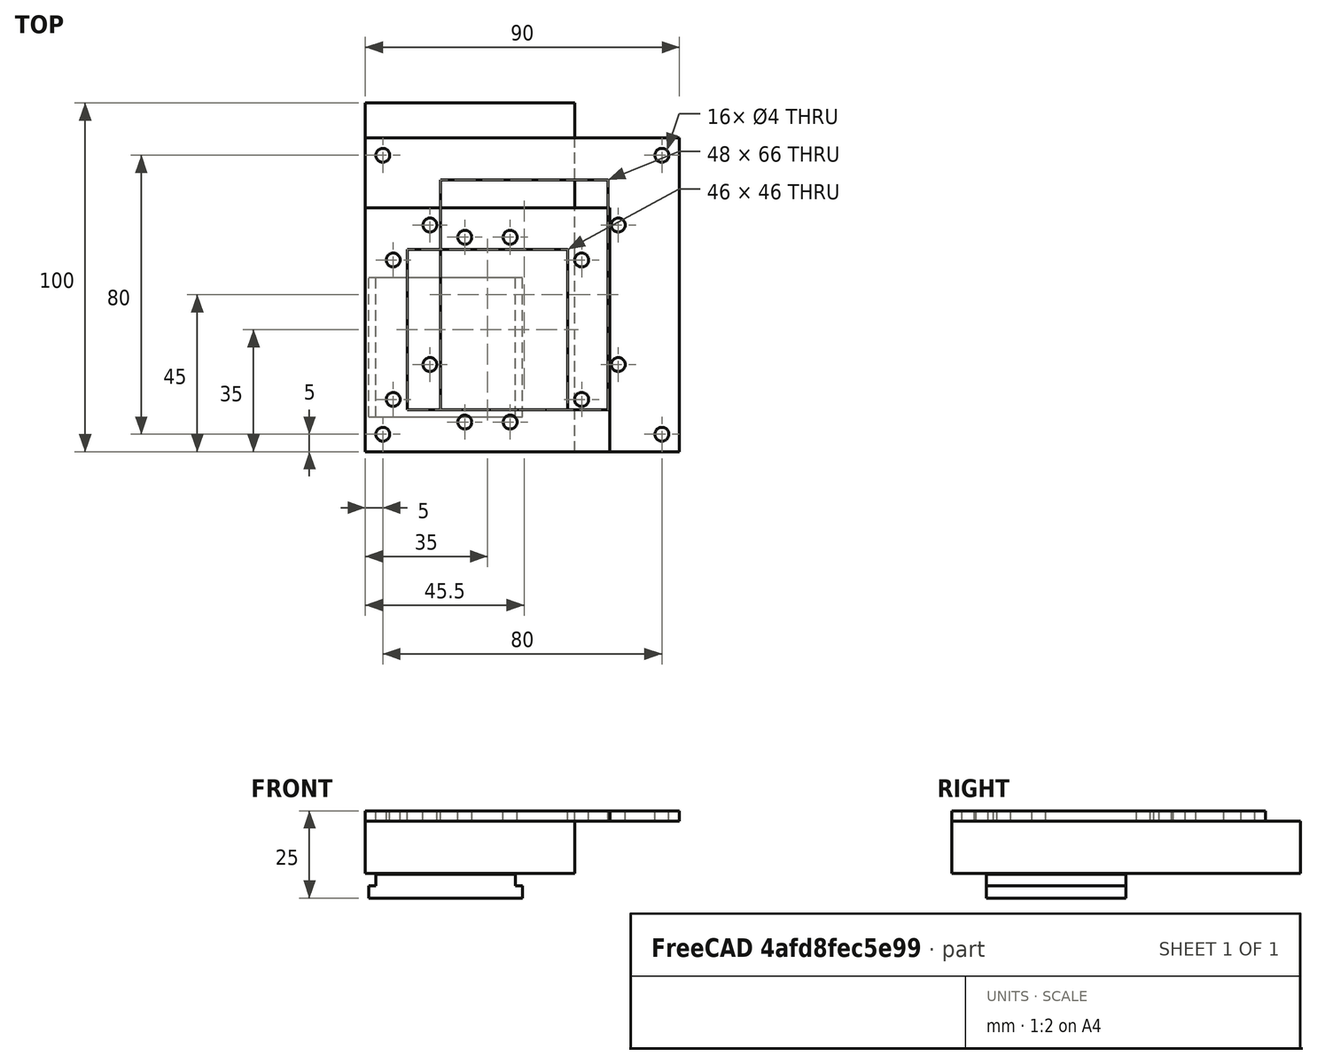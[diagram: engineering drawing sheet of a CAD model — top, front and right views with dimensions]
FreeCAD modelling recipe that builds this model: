
FCSTD DOCUMENT  (FreeCAD 0.18.4R)
Label: box_with_cone_less_holes
License: All rights reserved
LicenseURL: http://en.wikipedia.org/wiki/All_rights_reserved
objects: Part::FeaturePython×9, Part::Box×8, Path::FeaturePython×7, Part::Cylinder×6, Part::Cut×6, Part::MultiFuse×4, App::Part×4, Part::Cone×2, Part::Fuse×1, App::FeaturePython×1, App::DocumentObjectGroup×1, Path::FeatureCompoundPython×1
note: 39 computed .brp shape members not serialized (recipe doc carries the construction recipe); baked Part::Feature solids carry a one-line shape summary decoded from their .brp

FEATURE [Part::Box] Box  label="Cube"
  AttacherType = Attacher::AttachEngine3D
  Height = 15
  Length = 46
  Placement = pos=(0,0,-15) rot=(0,0,1;0rad)
  Width = 60
FEATURE [Part::Cone] Cone  label="top cone"
  Angle = 360
  AttacherType = Attacher::AttachEngine3D
  Height = 7
  Placement = pos=(0,0,-7) rot=(0,0,1;0rad)
  Radius1 = 2.8
  Radius2 = 3
FEATURE [Part::Cone] Cone001  label="bottom cone"
  Angle = 360
  AttacherType = Attacher::AttachEngine3D
  Height = 12
  Placement = pos=(0,0,-19) rot=(0,0,1;3.14159rad)
  Radius1 = 1.2
  Radius2 = 2.8
  Support = -> [Cone]
FEATURE [Part::Cylinder] Cylinder
  Angle = 360
  AttacherType = Attacher::AttachEngine3D
  Height = 30
  Placement = pos=(0,0,-20) rot=(0,0,1;0rad)
  Radius = 1.65
FEATURE [Part::FeaturePython] Array001  # Draft array (typed FeaturePython)
  Angle = 360
  ArrayType = 0
  Axis = (0,0,1)
  Base = -> Cylinder
  Center = (0,0,0)
  Fuse = false
  IntervalAxis = (0,0,0)
  IntervalX = (38,0,0)
  IntervalY = (0,13,0)
  IntervalZ = (0,0,1)
  NumberPolar = 1
  NumberX = 2
  NumberY = 3
  NumberZ = 1
  Placement = pos=(4,17,0) rot=(0,0,1;0rad)
FEATURE [Part::Cylinder] Cylinder001
  Angle = 360
  AttacherType = Attacher::AttachEngine3D
  Height = 30
  Placement = pos=(0,0,-20) rot=(0,0,1;0rad)
  Radius = 1.65
FEATURE [Part::FeaturePython] Array002  # Draft array (typed FeaturePython)
  Angle = 360
  ArrayType = 0
  Axis = (0,0,1)
  Base = -> Cylinder001
  Center = (0,0,0)
  Fuse = false
  IntervalAxis = (0,0,0)
  IntervalX = (13,0,0)
  IntervalY = (0,53,0)
  IntervalZ = (0,0,1)
  NumberPolar = 1
  NumberX = 2
  NumberY = 2
  NumberZ = 1
  Placement = pos=(16.5,3.5,0) rot=(0,0,1;0rad)
FEATURE [Part::Fuse] Fusion
  Base = -> Cone001
  Placement = pos=(0,0,5) rot=(0,0,1;0rad)
  Tool = -> Cone
FEATURE [Part::FeaturePython] Array  label="cone array"  # Draft array (typed FeaturePython)
  Angle = 360
  ArrayType = 0
  Axis = (0,0,1)
  Base = -> Fusion
  Center = (0,0,0)
  Fuse = false
  IntervalAxis = (0,0,0)
  IntervalX = (13,0,0)
  IntervalY = (0,13,0)
  IntervalZ = (0,0,1)
  NumberPolar = 1
  NumberX = 3
  NumberY = 4
  NumberZ = 1
  Placement = pos=(10,10,0) rot=(0,0,1;0rad)
FEATURE [Part::Cut] Cut  label="cut cones"
  Base = -> Box
  Tool = -> Array
FEATURE [Part::Box] Box001  label="aluminium solid"
  AttacherType = Attacher::AttachEngine3D
  Height = 15
  Length = 100
  Placement = pos=(0,0,-15) rot=(0,0,1;0rad)
  Width = 60
FEATURE [App::FeaturePython] SetupSheet  # Path/CAM operation (typed FeaturePython)
  ClearanceHeightExpression = OpStockZMax+SetupSheet.ClearanceHeightOffset
  ClearanceHeightOffset = 5
  FinalDepthExpression = OpFinalDepth
  HorizRapid = 100
  SafeHeightExpression = OpStockZMax+SetupSheet.SafeHeightOffset
  SafeHeightOffset = 3
  StartDepthExpression = OpStartDepth
  StepDownExpression = OpToolDiameter
  VertRapid = 100
FEATURE [Path::FeaturePython] T2__drill_3  label="T2: drill 3"  # Path/CAM operation (typed FeaturePython)
  HorizFeed = 0.5
  HorizRapid = 100
  SpindleDir = 0
  SpindleSpeed = 1000
  ToolNumber = 2
  VertFeed = 0.5
  VertRapid = 100
  expr: HorizRapid = SetupSheet.HorizRapid
  expr: VertRapid = SetupSheet.VertRapid
FEATURE [Path::FeaturePython] T4__endmill_2mm  label="T4: endmill 2mm"  # Path/CAM operation (typed FeaturePython)
  HorizFeed = 0.5
  HorizRapid = 100
  SpindleDir = 0
  SpindleSpeed = 1000
  ToolNumber = 4
  VertFeed = 0.5
  VertRapid = 100
  expr: HorizRapid = SetupSheet.HorizRapid
  expr: VertRapid = SetupSheet.VertRapid
FEATURE [Part::FeaturePython] Clone004  label="Stock-solid"  # Draft clone (typed FeaturePython)
  AttacherType = Attacher::AttachEngine3D
  Fuse = false
  Objects = -> [Box001]
  PathResource = Stock
  Placement = pos=(60,0,-15) rot=(0,0,1;1.5708rad)
  Scale = (1,1,1)
  StockType = Unknown
FEATURE [Path::FeaturePython] Contour  # Path/CAM operation (typed FeaturePython)
  Active = false
  AreaParams:
    Tolerance = 1e-07
    FitArcs = True
    Simplify = False
    CleanDistance = 0.0
    Accuracy = 0.01
    Unit = 1.0
    MinArcPoints = 4
    MaxArcPoints = 100
    ClipperScale = 10000000.0
    Fill = 0
    Coplanar = 2
    Reorient = True
    Outline = False
    Explode = False
    OpenMode = 0
    Deflection = 0.01
    SubjectFill = 0
    ClipFill = 0
    Offset = 1.0
    ExtraPass = 0
    Stepover = 0.0
    LastStepover = 0.0
    JoinType = 1
    EndType = 0
    MiterLimit = 2.0
    RoundPrecision = 0.0
    PocketMode = 0
    ToolRadius = 1.0
    PocketExtraOffset = 0.0
    PocketStepover = 0.0
    PocketLastStepover = 0.0
    FromCenter = False
    Angle = 45.0
    AngleShift = 0.0
    Shift = 0.0
    Thicken = False
    SectionCount = -1
    Stepdown = 1.0
    SectionOffset = 0.0
    SectionTolerance = 1e-06
    SectionMode = 2
    Project = False
  ClearanceHeight = 5
  Direction = 0
  FinalDepth = -16
  JoinType = 1
  MiterLimit = 0.1
  OffsetExtra = 0
  OpFinalDepth = -15
  OpStartDepth = 0
  OpStockZMax = 0
  OpStockZMin = -15
  OpToolDiameter = 2
  PathParams = {'orientation': 1, 'feedrate': 0.5, 'feedrate_v': 0.5, 'verbose': True, 'resume_height': 3.0, 'retraction': 5.0, 'return_end': True, 'preamble': False}
  SafeHeight = 3
  Side = 0
  StartDepth = 0
  StartPoint = (0,0,0)
  StepDown = 1
  ToolController = -> T4__endmill_2mm
  UseComp = true
  UseStartPoint = false
  expr: ClearanceHeight = OpStockZMax + SetupSheet.ClearanceHeightOffset
  expr: SafeHeight = OpStockZMax + SetupSheet.SafeHeightOffset
  expr: StartDepth = OpStartDepth
FEATURE [Part::Box] Box002  label="peltier"
  AttacherType = Attacher::AttachEngine3D
  Height = 3.3
  Length = 40
  Width = 40
FEATURE [Part::Box] Box003  label="radiator"
  AttacherType = Attacher::AttachEngine3D
  Height = 3.5
  Length = 44
  Placement = pos=(-2,0,-3.5) rot=(0,0,1;0rad)
  Width = 40
FEATURE [Part::Box] Box004  label="Cube001"
  AttacherType = Attacher::AttachEngine3D
  Height = 3
  Length = 90
  Width = 90
FEATURE [Part::Cylinder] Cylinder002  label="ring bolt hole"
  Angle = 360
  AttacherType = Attacher::AttachEngine3D
  Height = 50
  Radius = 2
FEATURE [Part::FeaturePython] Array003  label="ring holes array"  # Draft array (typed FeaturePython)
  Angle = 360
  ArrayType = 0
  Axis = (0,0,1)
  Base = -> Cylinder002
  Center = (0,0,0)
  Fuse = false
  IntervalAxis = (0,0,0)
  IntervalX = (80,0,0)
  IntervalY = (0,80,0)
  IntervalZ = (0,0,1)
  NumberPolar = 1
  NumberX = 2
  NumberY = 2
  NumberZ = 1
  Placement = pos=(5,5,-25) rot=(0,0,1;0rad)
FEATURE [Part::Box] Box005  label="Cube002"
  AttacherType = Attacher::AttachEngine3D
  Height = 50
  Length = 48
  Placement = pos=(21.5,12,-20) rot=(0,0,1;0rad)
  Width = 66
FEATURE [Part::Cut] Cut002  label="radiator ring plate cut"
  Base = -> Box004
  Tool = -> Box005
FEATURE [Part::Box] Box006  label="Cube003"
  AttacherType = Attacher::AttachEngine3D
  Height = 3
  Length = 70
  Width = 70
FEATURE [Part::Box] Box007  label="Cube004"
  AttacherType = Attacher::AttachEngine3D
  Height = 50
  Length = 46
  Placement = pos=(12,12,-20) rot=(0,0,1;0rad)
  Width = 46
FEATURE [Part::Cut] Cut004  label="block attachment plate cut"
  Base = -> Box006
  Tool = -> Box007
FEATURE [Part::MultiFuse] Fusion003  label="peltier and radiator"
  Placement = pos=(3,10,-18.5) rot=(0,0,1;0rad)
  Shapes = -> [Box002,Box003]
FEATURE [Part::FeaturePython] Array007  label="radiator plate holes"  # Draft array (typed FeaturePython)
  Angle = 360
  ArrayType = 0
  Axis = (0,0,1)
  Center = (0,0,0)
  Fuse = false
  IntervalAxis = (0,0,0)
  IntervalX = (54,0,0)
  IntervalY = (0,40,0)
  IntervalZ = (0,0,1)
  NumberPolar = 1
  NumberX = 2
  NumberY = 2
  NumberZ = 1
  Placement = pos=(8,15,-19) rot=(0,0,1;0rad)
FEATURE [Part::FeaturePython] Array006  label="plate cone box hole array001"  # Draft array (typed FeaturePython)
  Angle = 360
  ArrayType = 0
  Axis = (0,0,1)
  Center = (0,0,0)
  Fuse = false
  IntervalAxis = (0,0,0)
  IntervalX = (13,0,0)
  IntervalY = (0,53,0)
  IntervalZ = (0,0,1)
  NumberPolar = 1
  NumberX = 2
  NumberY = 2
  NumberZ = 1
  Placement = pos=(28.5,8.5,-19) rot=(0,0,1;0rad)
FEATURE [Part::MultiFuse] Fusion004  label="block attachment holes"
  Shapes = -> [Array006,Array007]
FEATURE [Part::Cut] Cut005  label="block attachement all holes cut"
  Base = -> Cut004
  Tool = -> Fusion004
FEATURE [App::Part] Part002  label="block attachment part"
  Group = -> [Box006,Cut004,Box007,Array006,Array007,Fusion004,Cut005]
  Origin = -> Origin002
  Placement = pos=(-12,-5,-18) rot=(0,0,1;0rad)
FEATURE [Part::FeaturePython] Array008  label="radiator plate holes001"  # Draft array (typed FeaturePython)
  Angle = 360
  ArrayType = 0
  Axis = (0,0,1)
  Center = (0,0,0)
  Fuse = false
  IntervalAxis = (0,0,0)
  IntervalX = (54,0,0)
  IntervalY = (0,40,0)
  IntervalZ = (0,0,1)
  NumberPolar = 1
  NumberX = 2
  NumberY = 2
  NumberZ = 1
  Placement = pos=(18.5,25,-19) rot=(0,0,1;0rad)
FEATURE [Part::MultiFuse] Fusion002  label="holes union"
  Shapes = -> [Array003,Array008]
FEATURE [Part::Cut] Cut003  label="radiator block cut"
  Base = -> Cut002
  Tool = -> Fusion002
FEATURE [App::Part] Part  label="radiator block attachment part"
  Group = -> [Box004,Array003,Cut002,Cylinder002,Box005,Fusion002,Cut003]
  Origin = -> Origin
  Placement = pos=(-22.5,-15,-3) rot=(0,0,1;0rad)
FEATURE [Part::Cylinder] Cylinder003  label="ntc_1.8"
  Angle = 360
  AttacherType = Attacher::AttachEngine3D
  Height = 10
  Placement = pos=(30,17,-9) rot=(0,0,1;0rad)
  Radius = 0.9
FEATURE [Part::Cylinder] Cylinder004  label="ntc_2.35"
  Angle = 360
  AttacherType = Attacher::AttachEngine3D
  Height = 10
  Placement = pos=(30,43,-9) rot=(0,0,1;0rad)
  Radius = 1.175
FEATURE [Part::Cylinder] Cylinder005  label="ntc_3"
  Angle = 360
  AttacherType = Attacher::AttachEngine3D
  Height = 10
  Placement = pos=(16,17,-9) rot=(0,0,1;0rad)
  Radius = 1.5
FEATURE [Part::MultiFuse] Fusion001  label="hole union"
  Shapes = -> [Array001,Array002,Cylinder003,Cylinder004,Cylinder005]
FEATURE [Part::Cut] Cut001  label="All cut"
  Base = -> Cut
  Tool = -> Fusion001
FEATURE [Part::FeaturePython] Clone  label="Model-All cut"  # Draft clone (typed FeaturePython)
  AttacherType = Attacher::AttachEngine3D
  Fuse = false
  Objects = -> [Cut001]
  PathResource = Model
  Placement = pos=(60,0,0) rot=(0,0,1;1.5708rad)
  Scale = (1,1,1)
FEATURE [App::DocumentObjectGroup] Model
  Group = -> [Clone]
FEATURE [Path::FeaturePython] Pocket_3D  # Path/CAM operation (typed FeaturePython)
  Active = false
  AreaParams:
    Tolerance = 1e-07
    FitArcs = True
    Simplify = False
    CleanDistance = 0.0
    Accuracy = 0.01
    Unit = 1.0
    MinArcPoints = 4
    MaxArcPoints = 100
    ClipperScale = 10000000.0
    Fill = 0
    Coplanar = 0
    Reorient = True
    Outline = False
    Explode = False
    OpenMode = 0
    Deflection = 0.01
    SubjectFill = 0
    ClipFill = 0
    Offset = 0.0
    ExtraPass = 0
    Stepover = 0.0
    LastStepover = 0.0
    JoinType = 0
    EndType = 0
    MiterLimit = 2.0
    RoundPrecision = 0.0
    PocketMode = 3
    ToolRadius = 1.0
    PocketExtraOffset = 0.0
    PocketStepover = 2.0
    PocketLastStepover = 0.0
    FromCenter = True
    Angle = 45.0
    AngleShift = 0.0
    Shift = 0.0
    Thicken = False
    SectionCount = -1
    Stepdown = 1.0
    SectionOffset = 0.0
    SectionTolerance = 1e-06
    SectionMode = 2
    Project = False
  Base = -> [Clone]
  ClearanceHeight = 5
  CutMode = 0
  ExtraOffset = 0
  FinalDepth = -2
  FinishDepth = 0
  KeepToolDown = true
  MinTravel = false
  OffsetPattern = 2
  OpFinalDepth = -2
  OpStartDepth = 0
  OpStockZMax = 0
  OpStockZMin = -15
  OpToolDiameter = 2
  PathParams = {'orientation': 1, 'feedrate': 0.5, 'feedrate_v': 0.5, 'verbose': True, 'resume_height': 3.0, 'retraction': 5.0, 'return_end': True, 'preamble': False, 'threshold': 2.001, 'start': Vector (34.87061227627158, 37.332291129902295, -3.999999)}
  SafeHeight = 3
  StartAt = 0
  StartDepth = 0
  StartPoint = (0,0,0)
  StepDown = 0.25
  StepOver = 100
  ToolController = -> T4__endmill_2mm
  UseStartPoint = false
  ZigZagAngle = 45
  expr: ClearanceHeight = OpStockZMax + SetupSheet.ClearanceHeightOffset
  expr: SafeHeight = OpStockZMax + SetupSheet.SafeHeightOffset
  expr: FinalDepth = OpFinalDepth
  expr: StartDepth = OpStartDepth
FEATURE [Path::FeaturePython] Pocket_3D001  # Path/CAM operation (typed FeaturePython)
  Active = false
  AreaParams:
    Tolerance = 1e-07
    FitArcs = True
    Simplify = False
    CleanDistance = 0.0
    Accuracy = 0.01
    Unit = 1.0
    MinArcPoints = 4
    MaxArcPoints = 100
    ClipperScale = 10000000.0
    Fill = 0
    Coplanar = 0
    Reorient = True
    Outline = False
    Explode = False
    OpenMode = 0
    Deflection = 0.01
    SubjectFill = 0
    ClipFill = 0
    Offset = 0.0
    ExtraPass = 0
    Stepover = 0.0
    LastStepover = 0.0
    JoinType = 0
    EndType = 0
    MiterLimit = 2.0
    RoundPrecision = 0.0
    PocketMode = 3
    ToolRadius = 1.0
    PocketExtraOffset = -0.3
    PocketStepover = 2.0
    PocketLastStepover = 0.0
    FromCenter = False
    Angle = 45.0
    AngleShift = 0.0
    Shift = 0.0
    Thicken = False
    SectionCount = -1
    Stepdown = 1.0
    SectionOffset = 0.0
    SectionTolerance = 1e-06
    SectionMode = 2
    Project = False
  Base = -> [Clone]
  ClearanceHeight = 5
  CutMode = 0
  ExtraOffset = -0.3
  FinalDepth = -15
  FinishDepth = 0
  KeepToolDown = false
  MinTravel = false
  OffsetPattern = 2
  OpFinalDepth = -15
  OpStartDepth = 0
  OpStockZMax = 0
  OpStockZMin = -15
  OpToolDiameter = 2
  PathParams = {'orientation': 1, 'feedrate': 0.5, 'feedrate_v': 0.5, 'verbose': True, 'resume_height': 5.0, 'retraction': 5.0, 'return_end': True, 'preamble': False, 'start': Vector (0.0, 0.0, 0.0)}
  SafeHeight = 5
  StartAt = 1
  StartDepth = -0.5
  StartPoint = (0,0,0)
  StepDown = 0.5
  StepOver = 100
  ToolController = -> T4__endmill_2mm
  UseStartPoint = true
  ZigZagAngle = 45
  expr: ClearanceHeight = OpStockZMax + SetupSheet.ClearanceHeightOffset
  expr: FinalDepth = OpFinalDepth
FEATURE [Path::FeaturePython] Drilling  # Path/CAM operation (typed FeaturePython)
  Active = true
  AddTipLength = false
  Base = -> [Clone]
  ClearanceHeight = 5
  DwellEnabled = false
  DwellTime = 0
  FinalDepth = -15
  OpFinalDepth = 0
  OpStartDepth = 1
  OpStockZMax = 0
  OpStockZMin = -15
  OpToolDiameter = 3
  PeckDepth = 0
  PeckEnabled = false
  RetractHeight = 10
  ReturnLevel = 0
  SafeHeight = 3
  StartDepth = 1
  ToolController = -> T2__drill_3
  expr: ClearanceHeight = OpStockZMax + SetupSheet.ClearanceHeightOffset
  expr: SafeHeight = OpStockZMax + SetupSheet.SafeHeightOffset
  expr: StartDepth = OpStartDepth
FEATURE [Path::FeatureCompoundPython] Operations  # Path/CAM operation (typed FeaturePython)
  Group = -> [Contour,Pocket_3D,Pocket_3D001,Drilling]
  UsePlacements = false
FEATURE [Path::FeaturePython] Job  # Path/CAM operation (typed FeaturePython)
  GeometryTolerance = 0.01
  Model = -> Model
  Operations = -> Operations
  PostProcessor = 1
  PostProcessorOutputFile = <userpath>/work/roborep/gcode
  SetupSheet = -> SetupSheet
  Stock = -> Clone004
  ToolController = -> [T2__drill_3,T4__endmill_2mm]
FEATURE [App::Part] Part001  label="cone block"
  Group = -> [Cone,Cylinder001,Fusion,Cut,Fusion001,Array001,Cone001,Box,Cylinder,Array,Array002,Cut001,Cylinder003,Cylinder004,Cylinder005]
  Origin = -> Origin001
FEATURE [App::Part] Part003  label="Part"
  Group = -> [Part001,Box003,Box002,Fusion003,Part002,Part,Box001]
  Origin = -> Origin003
  Placement = pos=(60,0,0) rot=(0,0,1;1.5708rad)
